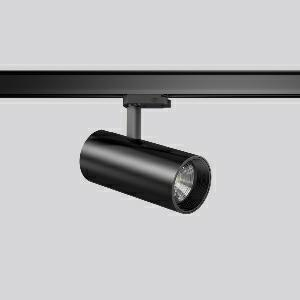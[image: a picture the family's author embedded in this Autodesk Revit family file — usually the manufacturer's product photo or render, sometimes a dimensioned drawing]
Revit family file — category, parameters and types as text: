
# Revit family: deecos_s_mini_742208_003_3_76_b46e
name_source: partatom
category: Lighting Fixtures
units: mm (PartAtom-declared; Revit-internal decimal feet)

## family parameters
Cut with Voids When Loaded = No
Host = Face
Light Source = No
Part Type = Normal
Room Calculation Point = No
Round Connector Dimension = Use Diameter
Shared = No

## types (1)
- DEECOS S mini (1 x LED Modul 935, 2900 lm, 3500)
    Apparent Load = 29 VA
    Approval mark = CE
    CIE Flux Codes = 98 100 100 100 100
    Color Rendering = 92
    Color Temperature = 3500
    Default Elevation = 1800 mm
    Description = Series: DEECOS S mini
LED surface-mounted projector in modern design with no visible cooling ribs. Housing: die-cast aluminium, powder-coated. Rotation range: 356°. Swivel range: 90°. Black plastic ring and recessed LED to prevent glare from the side. Optical assembly with lens made of plastic (polycarbonate) for the best homogeneous light distribution - can be changed without tools. Best colour rendering index Ra>90. With adapter for RZB 3-circuit DALI tracks. Suitable for Track on ceiling, Wall track. High quality converter without flickering and stroboscopic effect. The following accessories can be mounted without use of tools: interchangeable lenses, decorative glasses, honeycomb louvre, clear and frosted diffusers, white interchangeable plastic ring. 
Colour: deep black, matt (RAL 9005)
Diameter: 87 mm
Height: 214 mm
Lamp: LED
Socket: without socket
Colour temperature: 3500K
Colour rendering index (CRI): 92
System power: 29 W
Rated luminous flux: 2900 lm
Luminous efficiency: 100 lm/W
Control gear: Converter, dimmable, DALI
Protection class: I
Type of protection: IP 20
    Height = 214 mm
    Lamp = 1 x LED Modul 935
    Lamp Light Flux = 2900 lm
    Lamp count = 1
    Length = 87 mm
    Lifetime = 50000 h
    Luminous efficacy = 100 lm/W
    Manufacturer = RZB
    ModVariant = No
    Model = 742208.003.3.76
    Mounting Place = Ceiling
    Mounting Type = Rail mounted
    Number of Poles = 1
    OnlyDefault = Yes
    Power Factor = 1
    Product Name = DEECOS S mini
    Product group = Track mounted projectors
    ProductGroupID = 301
    Protection Class = Protection class I
    Protection Degree = IP 20
    RLX_Detail_Level = 1
    RLX_Emergency_Light_Flux = 0 lm
    RLX_Emergency_Type = 0
    RLX_Emergency_Type_DB = No
    RlxData = <blob elided: 38737 chars, md5=826eed00>
    Socket = socket
    Standby Power = 0 W
    System Light Flux = 2900 lm
    System Power = 29 W
    Type Comments = Product without accessories
    Type Image = 741930.003.jpg
    URL = http://relux.com
    VarID = ---
    Voltage = 230 V
    Voltage Range = 220-240 V
    Weight = 0.00 kg
    Width = 0 mm  [stored 0 ft]

note: [stored X ft] marks values corroborated as IEEE doubles in the binary element streams (Revit-internal decimal feet)

## geometry (parser evidence)
native form markers: Blend x4, Sweep x12
no freeform markers — native parametric forms only
